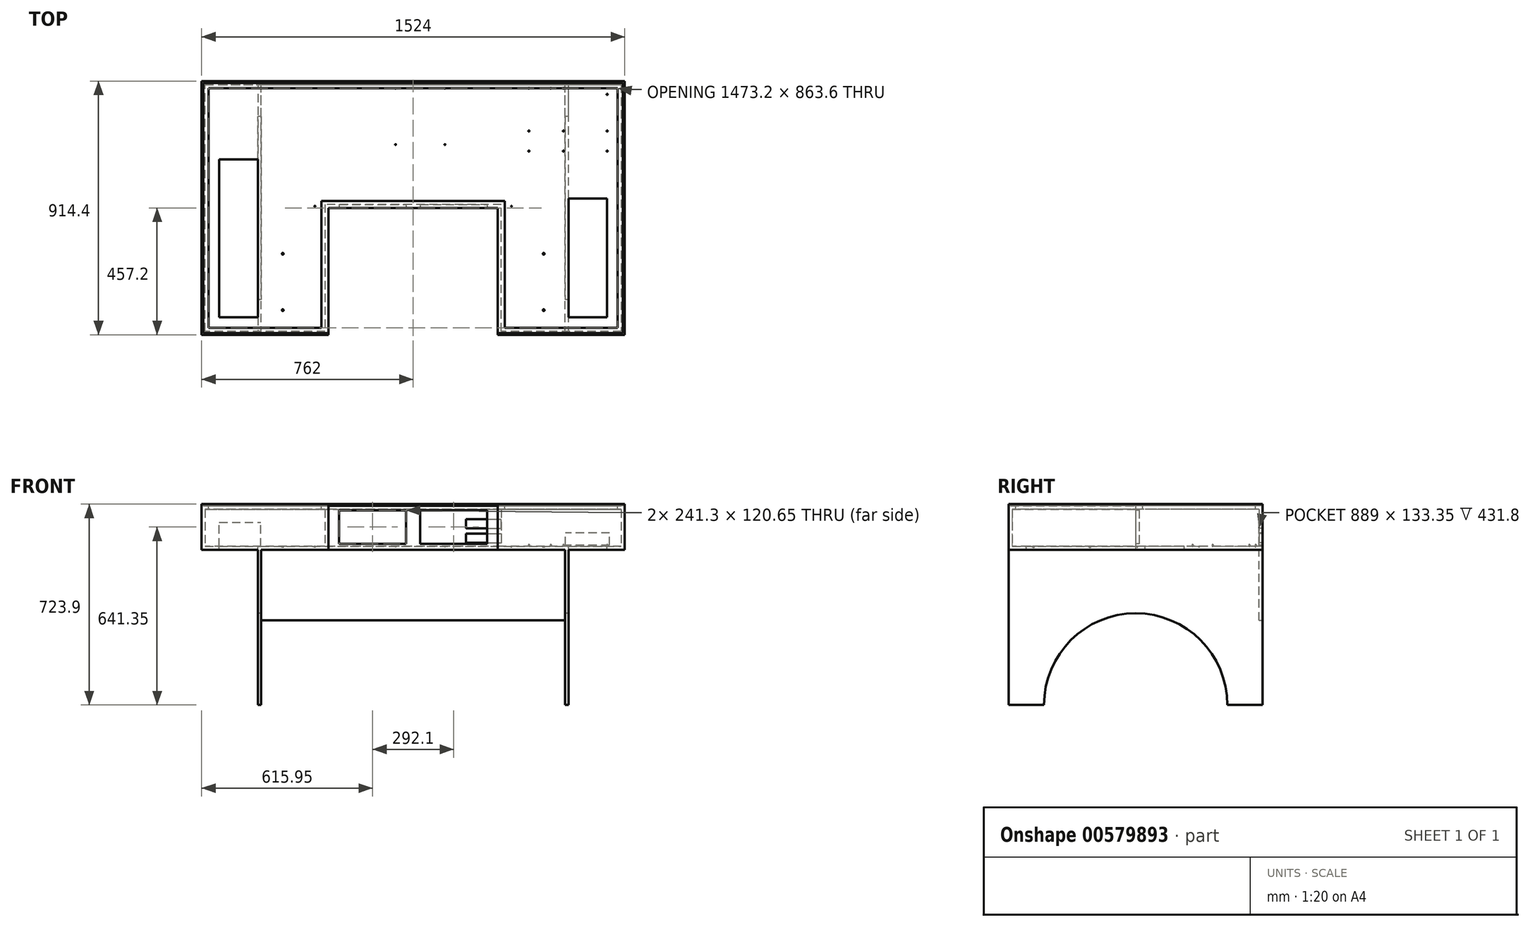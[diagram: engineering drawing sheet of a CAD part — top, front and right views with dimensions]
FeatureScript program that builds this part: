
annotation { "Feature Type Name" : "Feature", "Feature Type Description" : "" }
export const myFeature = defineFeature(function(context is Context, id is Id, definition is map)
    precondition{}
    {
        {
            var Q0;
            Q0=qCreatedBy(makeId("Top.planeOp"),FACE);
            var sketch = newSketch(context, id + "F0", { "sketchPlane" : qUnion([Q0])});
            skLineSegment(sketch, "E0.top", {"start": v(0, 914.4) * mm, "end": v(-1524, 914.4) * mm});
            skLineSegment(sketch, "E0.left", {"start": v(0, 0) * mm, "end": v(0, 914.4) * mm});
            skLineSegment(sketch, "E0.right", {"start": v(-1524, 0) * mm, "end": v(-1524, 914.4) * mm});
            skLineSegment(sketch, "E1.top", {"start": v(-1066.8, 457.2) * mm, "end": v(-457.2, 457.2) * mm});
            skLineSegment(sketch, "E1.left", {"start": v(-1066.8, 0) * mm, "end": v(-1066.8, 457.2) * mm});
            skLineSegment(sketch, "E1.right", {"start": v(-457.2, 0) * mm, "end": v(-457.2, 457.2) * mm});
            skLineSegment(sketch, "E2", {"start": v(-1524, 0) * mm, "end": v(-1066.8, 0) * mm});
            skLineSegment(sketch, "E3", {"start": v(-457.2, 0) * mm, "end": v(0, 0) * mm});
            skSolve(sketch);
        }
        {
            var Q0;
            Q0 = qSketchRegion(id + "F0", true);
            extrude(context, id + "F1", {"entities" : qUnion([Q0]), "depth" : 12.7 * mm, "offsetDistance" : 25.4 * mm});
        }
        {
            var Q0;
            Q0=makeQuery(id+"F1.opExtrude","CAP_FACE",FACE,{"disambiguationData":[OSD([sQuery(id+"F0.wireOp",EDGE,"E0.top"),sQuery(id+"F0.wireOp",EDGE,"E0.left"),sQuery(id+"F0.wireOp",EDGE,"E0.right"),sQuery(id+"F0.wireOp",EDGE,"E1.top"),sQuery(id+"F0.wireOp",EDGE,"E1.left"),sQuery(id+"F0.wireOp",EDGE,"E1.right"),sQuery(id+"F0.wireOp",EDGE,"E2"),sQuery(id+"F0.wireOp",EDGE,"E3")])],"isStart":false});
            var sketch = newSketch(context, id + "F2", { "sketchPlane" : qUnion([Q0])});
            skLineSegment(sketch, "E4", {"start": v(0, 0) * mm, "end": v(0, 914.4) * mm});
            skLineSegment(sketch, "E5", {"start": v(0, 914.4) * mm, "end": v(-1524, 914.4) * mm});
            skLineSegment(sketch, "E6", {"start": v(-1524, 914.4) * mm, "end": v(-1524, 0) * mm});
            skLineSegment(sketch, "E7", {"start": v(-1524, 0) * mm, "end": v(-1066.8, 0) * mm});
            skLineSegment(sketch, "E8", {"start": v(-1066.8, 0) * mm, "end": v(-1066.8, 457.2) * mm});
            skLineSegment(sketch, "E9", {"start": v(-1066.8, 457.2) * mm, "end": v(-457.2, 457.2) * mm});
            skLineSegment(sketch, "E10", {"start": v(-457.2, 457.2) * mm, "end": v(-457.2, 0) * mm});
            skLineSegment(sketch, "E11", {"start": v(-457.2, 0) * mm, "end": v(0, 0) * mm});
            skLineSegment(sketch, "E12", {"start": v(-12.7, 12.7) * mm, "end": v(-444.5, 12.7) * mm});
            skLineSegment(sketch, "E13", {"start": v(-444.5, 12.7) * mm, "end": v(-444.5, 469.9) * mm});
            skLineSegment(sketch, "E14", {"start": v(-444.5, 469.9) * mm, "end": v(-1079.5, 469.9) * mm});
            skLineSegment(sketch, "E15", {"start": v(-1079.5, 469.9) * mm, "end": v(-1079.5, 12.7) * mm});
            skLineSegment(sketch, "E16", {"start": v(-1079.5, 12.7) * mm, "end": v(-1511.3, 12.7) * mm});
            skLineSegment(sketch, "E17", {"start": v(-1511.3, 12.7) * mm, "end": v(-1511.3, 901.7) * mm});
            skLineSegment(sketch, "E18", {"start": v(-1511.3, 901.7) * mm, "end": v(-12.7, 901.7) * mm});
            skLineSegment(sketch, "E19", {"start": v(-12.7, 901.7) * mm, "end": v(-12.7, 12.7) * mm});
            skSolve(sketch);
        }
        {
            var Q0;
            Q0 = qSketchRegion(id + "F2", true);
            extrude(context, id + "F3", {"entities" : qUnion([Q0]), "operationType" : NewBodyOperationType.ADD, "depth" : 152.4 * mm, "offsetDistance" : 25.4 * mm});
        }
        {
            var Q0;
            Q0=makeQuery(id+"F1.opExtrude","CAP_FACE",FACE,{"disambiguationData":[OSD([sQuery(id+"F0.wireOp",EDGE,"E0.top"),sQuery(id+"F0.wireOp",EDGE,"E0.left"),sQuery(id+"F0.wireOp",EDGE,"E0.right"),sQuery(id+"F0.wireOp",EDGE,"E1.top"),sQuery(id+"F0.wireOp",EDGE,"E1.left"),sQuery(id+"F0.wireOp",EDGE,"E1.right"),sQuery(id+"F0.wireOp",EDGE,"E2"),sQuery(id+"F0.wireOp",EDGE,"E3")])],"isStart":false});
            var sketch = newSketch(context, id + "F4", { "sketchPlane" : qUnion([Q0])});
            skCircle(sketch, "E20", {"center": v(-345.44, 889.43) * mm, "radius": 1.98 * mm});
            skCircle(sketch, "E21", {"center": v(-345.44, 734.5) * mm, "radius": 1.98 * mm});
            skCircle(sketch, "E22", {"center": v(-345.44, 662.1) * mm, "radius": 1.98 * mm});
            skCircle(sketch, "E23", {"center": v(-266.7, 889.43) * mm, "radius": 1.98 * mm});
            skCircle(sketch, "E24", {"center": v(-220.98, 889.43) * mm, "radius": 1.98 * mm});
            skCircle(sketch, "E25", {"center": v(-220.98, 734.5) * mm, "radius": 1.98 * mm});
            skCircle(sketch, "E26", {"center": v(-220.98, 662.1) * mm, "radius": 1.98 * mm});
            skCircle(sketch, "E27", {"center": v(-63.5, 866.57) * mm, "radius": 1.98 * mm});
            skCircle(sketch, "E28", {"center": v(-63.5, 734.5) * mm, "radius": 1.98 * mm});
            skCircle(sketch, "E29", {"center": v(-63.5, 662.1) * mm, "radius": 1.98 * mm});
            skSolve(sketch);
        }
        {
            var Q0;
            Q0=makeQuery(id+"F4.imprint","IMPRINT",FACE,{"disambiguationData":[TD([[makeQuery(id+"F4.imprint","IMPRINT",EDGE,{"derivedFrom":sQuery(id+"F4.wireOp",EDGE,"E20")}),1.0]])]});
            var Q1;
            Q1=makeQuery(id+"F4.imprint","IMPRINT",FACE,{"disambiguationData":[TD([[makeQuery(id+"F4.imprint","IMPRINT",EDGE,{"derivedFrom":sQuery(id+"F4.wireOp",EDGE,"E23")}),1.0]])]});
            var Q2;
            Q2=makeQuery(id+"F4.imprint","IMPRINT",FACE,{"disambiguationData":[TD([[makeQuery(id+"F4.imprint","IMPRINT",EDGE,{"derivedFrom":sQuery(id+"F4.wireOp",EDGE,"E24")}),1.0]])]});
            var Q3;
            Q3=makeQuery(id+"F4.imprint","IMPRINT",FACE,{"disambiguationData":[TD([[makeQuery(id+"F4.imprint","IMPRINT",EDGE,{"derivedFrom":sQuery(id+"F4.wireOp",EDGE,"E27")}),1.0]])]});
            var Q4;
            Q4=makeQuery(id+"F4.imprint","IMPRINT",FACE,{"disambiguationData":[TD([[makeQuery(id+"F4.imprint","IMPRINT",EDGE,{"derivedFrom":sQuery(id+"F4.wireOp",EDGE,"E28")}),1.0]])]});
            var Q5;
            Q5=makeQuery(id+"F4.imprint","IMPRINT",FACE,{"disambiguationData":[TD([[makeQuery(id+"F4.imprint","IMPRINT",EDGE,{"derivedFrom":sQuery(id+"F4.wireOp",EDGE,"E25")}),1.0]])]});
            var Q6;
            Q6=makeQuery(id+"F4.imprint","IMPRINT",FACE,{"disambiguationData":[TD([[makeQuery(id+"F4.imprint","IMPRINT",EDGE,{"derivedFrom":sQuery(id+"F4.wireOp",EDGE,"E21")}),1.0]])]});
            var Q7;
            Q7=makeQuery(id+"F4.imprint","IMPRINT",FACE,{"disambiguationData":[TD([[makeQuery(id+"F4.imprint","IMPRINT",EDGE,{"derivedFrom":sQuery(id+"F4.wireOp",EDGE,"E22")}),1.0]])]});
            var Q8;
            Q8=makeQuery(id+"F4.imprint","IMPRINT",FACE,{"disambiguationData":[TD([[makeQuery(id+"F4.imprint","IMPRINT",EDGE,{"derivedFrom":sQuery(id+"F4.wireOp",EDGE,"E26")}),1.0]])]});
            var Q9;
            Q9=makeQuery(id+"F4.imprint","IMPRINT",FACE,{"disambiguationData":[TD([[makeQuery(id+"F4.imprint","IMPRINT",EDGE,{"derivedFrom":sQuery(id+"F4.wireOp",EDGE,"E29")}),1.0]])]});
            extrude(context, id + "F5", {"entities" : qUnion([Q0, Q1, Q2, Q3, Q4, Q5, Q6, Q7, Q8, Q9]), "operationType" : NewBodyOperationType.ADD, "depth" : 6.35 * mm, "offsetDistance" : 25.4 * mm});
        }
        {
            var Q0;
            Q0=makeQuery(id+"F3.opExtrude","SWEPT_FACE",FACE,{"disambiguationData":[OSD([sQuery(id+"F2.wireOp",EDGE,"E18")])]});
            var sketch = newSketch(context, id + "F6", { "sketchPlane" : qUnion([Q0])});
            skLineSegment(sketch, "E30.bottom", {"start": v(-54.71, 16.81) * mm, "end": v(-213.46, 16.81) * mm});
            skLineSegment(sketch, "E30.top", {"start": v(-54.71, 61.26) * mm, "end": v(-213.46, 61.26) * mm});
            skLineSegment(sketch, "E30.left", {"start": v(-54.71, 16.81) * mm, "end": v(-54.71, 61.26) * mm});
            skLineSegment(sketch, "E30.right", {"start": v(-213.46, 16.81) * mm, "end": v(-213.46, 61.26) * mm});
            skSolve(sketch);
        }
        {
            var Q0;
            Q0 = qSketchRegion(id + "F6", true);
            extrude(context, id + "F7", {"entities" : qUnion([Q0]), "operationType" : NewBodyOperationType.REMOVE, "oppositeDirection" : true, "depth" : 25.4 * mm, "offsetDistance" : 25.4 * mm});
        }
        {
            var Q0;
            Q0=makeQuery(id+"F3.opExtrude","SWEPT_FACE",FACE,{"disambiguationData":[OSD([sQuery(id+"F2.wireOp",EDGE,"E18")])]});
            var sketch = newSketch(context, id + "F8", { "sketchPlane" : qUnion([Q0])});
            skLineSegment(sketch, "E31.bottom", {"start": v(-571.5, 58.74) * mm, "end": v(-444.5, 58.74) * mm});
            skLineSegment(sketch, "E31.top", {"start": v(-571.5, 25.4) * mm, "end": v(-444.5, 25.4) * mm});
            skLineSegment(sketch, "E31.left", {"start": v(-571.5, 58.74) * mm, "end": v(-571.5, 25.4) * mm});
            skLineSegment(sketch, "E31.right", {"start": v(-444.5, 58.74) * mm, "end": v(-444.5, 25.4) * mm});
            skLineSegment(sketch, "E32.bottom", {"start": v(-571.5, 77.79) * mm, "end": v(-444.5, 77.79) * mm});
            skLineSegment(sketch, "E32.top", {"start": v(-571.5, 111.13) * mm, "end": v(-444.5, 111.13) * mm});
            skLineSegment(sketch, "E32.left", {"start": v(-571.5, 77.79) * mm, "end": v(-571.5, 111.13) * mm});
            skLineSegment(sketch, "E32.right", {"start": v(-444.5, 77.79) * mm, "end": v(-444.5, 111.13) * mm});
            skSolve(sketch);
        }
        {
            var Q0;
            Q0 = qSketchRegion(id + "F8", true);
            extrude(context, id + "F9", {"entities" : qUnion([Q0]), "operationType" : NewBodyOperationType.REMOVE, "oppositeDirection" : true, "depth" : 25.4 * mm, "offsetDistance" : 25.4 * mm});
        }
        {
            var Q0;
            Q0=makeQuery(id+"F1.opExtrude","CAP_FACE",FACE,{"disambiguationData":[OSD([sQuery(id+"F0.wireOp",EDGE,"E0.top"),sQuery(id+"F0.wireOp",EDGE,"E0.left"),sQuery(id+"F0.wireOp",EDGE,"E0.right"),sQuery(id+"F0.wireOp",EDGE,"E1.top"),sQuery(id+"F0.wireOp",EDGE,"E1.left"),sQuery(id+"F0.wireOp",EDGE,"E1.right"),sQuery(id+"F0.wireOp",EDGE,"E2"),sQuery(id+"F0.wireOp",EDGE,"E3")])],"isStart":false});
            var sketch = newSketch(context, id + "F10", { "sketchPlane" : qUnion([Q0])});
            skCircle(sketch, "E33", {"center": v(-647.7, 889) * mm, "radius": 1.59 * mm});
            skCircle(sketch, "E34", {"center": v(-647.7, 685.8) * mm, "radius": 1.59 * mm});
            skCircle(sketch, "E35", {"center": v(-825.5, 889) * mm, "radius": 1.59 * mm});
            skCircle(sketch, "E36", {"center": v(-825.5, 685.8) * mm, "radius": 1.59 * mm});
            skSolve(sketch);
        }
        {
            var Q0;
            Q0 = qSketchRegion(id + "F10", true);
            extrude(context, id + "F11", {"entities" : qUnion([Q0]), "operationType" : NewBodyOperationType.REMOVE, "oppositeDirection" : true, "depth" : 2.54 * mm, "offsetDistance" : 25.4 * mm});
        }
        {
            var Q0;
            Q0=makeQuery(id+"F1.opExtrude","CAP_FACE",FACE,{"disambiguationData":[OSD([sQuery(id+"F0.wireOp",EDGE,"E0.top"),sQuery(id+"F0.wireOp",EDGE,"E0.left"),sQuery(id+"F0.wireOp",EDGE,"E0.right"),sQuery(id+"F0.wireOp",EDGE,"E1.top"),sQuery(id+"F0.wireOp",EDGE,"E1.left"),sQuery(id+"F0.wireOp",EDGE,"E1.right"),sQuery(id+"F0.wireOp",EDGE,"E2"),sQuery(id+"F0.wireOp",EDGE,"E3")])],"isStart":false});
            var sketch = newSketch(context, id + "F12", { "sketchPlane" : qUnion([Q0])});
            skLineSegment(sketch, "E37.bottom", {"start": v(-1460.5, 631.75) * mm, "end": v(-1321.85, 631.75) * mm});
            skLineSegment(sketch, "E37.top", {"start": v(-1460.5, 63.5) * mm, "end": v(-1321.85, 63.5) * mm});
            skLineSegment(sketch, "E37.left", {"start": v(-1460.5, 631.75) * mm, "end": v(-1460.5, 63.5) * mm});
            skLineSegment(sketch, "E37.right", {"start": v(-1321.85, 631.75) * mm, "end": v(-1321.85, 63.5) * mm});
            skLineSegment(sketch, "E38.bottom", {"start": v(-202.15, 491.75) * mm, "end": v(-63.5, 491.75) * mm});
            skLineSegment(sketch, "E38.top", {"start": v(-202.15, 63.5) * mm, "end": v(-63.5, 63.5) * mm});
            skLineSegment(sketch, "E38.left", {"start": v(-202.15, 491.75) * mm, "end": v(-202.15, 63.5) * mm});
            skLineSegment(sketch, "E38.right", {"start": v(-63.5, 491.75) * mm, "end": v(-63.5, 63.5) * mm});
            skSolve(sketch);
        }
        {
            var Q0;
            Q0 = qSketchRegion(id + "F12", true);
            extrude(context, id + "F13", {"entities" : qUnion([Q0]), "operationType" : NewBodyOperationType.REMOVE, "endBound" : BoundingType.THROUGH_ALL, "oppositeDirection" : true, "depth" : 25.4 * mm, "offsetDistance" : 25.4 * mm});
        }
        {
            var Q0;
            Q0=makeQuery(id+"F1.opExtrude","CAP_FACE",FACE,{"disambiguationData":[OSD([sQuery(id+"F0.wireOp",EDGE,"E0.top"),sQuery(id+"F0.wireOp",EDGE,"E0.left"),sQuery(id+"F0.wireOp",EDGE,"E0.right"),sQuery(id+"F0.wireOp",EDGE,"E1.top"),sQuery(id+"F0.wireOp",EDGE,"E1.left"),sQuery(id+"F0.wireOp",EDGE,"E1.right"),sQuery(id+"F0.wireOp",EDGE,"E2"),sQuery(id+"F0.wireOp",EDGE,"E3")])],"isStart":false});
            var sketch = newSketch(context, id + "F14", { "sketchPlane" : qUnion([Q0])});
            skCircle(sketch, "E39", {"center": v(-1231.9, 88.9) * mm, "radius": 3.18 * mm});
            skCircle(sketch, "E40", {"center": v(-1231.9, 292.1) * mm, "radius": 3.18 * mm});
            skCircle(sketch, "E41", {"center": v(-292.1, 292.1) * mm, "radius": 3.18 * mm});
            skCircle(sketch, "E42", {"center": v(-292.1, 88.9) * mm, "radius": 3.18 * mm});
            skSolve(sketch);
        }
        {
            var Q0;
            Q0 = qSketchRegion(id + "F14", true);
            extrude(context, id + "F15", {"entities" : qUnion([Q0]), "operationType" : NewBodyOperationType.REMOVE, "oppositeDirection" : true, "depth" : 3.17 * mm, "offsetDistance" : 25.4 * mm});
        }
        {
            var Q0;
            Q0=makeQuery(id+"F1.opExtrude","CAP_FACE",FACE,{"disambiguationData":[OSD([sQuery(id+"F0.wireOp",EDGE,"E0.top"),sQuery(id+"F0.wireOp",EDGE,"E0.left"),sQuery(id+"F0.wireOp",EDGE,"E0.right"),sQuery(id+"F0.wireOp",EDGE,"E1.top"),sQuery(id+"F0.wireOp",EDGE,"E1.left"),sQuery(id+"F0.wireOp",EDGE,"E1.right"),sQuery(id+"F0.wireOp",EDGE,"E2"),sQuery(id+"F0.wireOp",EDGE,"E3")])],"isStart":false});
            var sketch = newSketch(context, id + "F16", { "sketchPlane" : qUnion([Q0])});
            skCircle(sketch, "E43", {"center": v(-1116.01, 463.55) * mm, "radius": 1.59 * mm});
            skCircle(sketch, "E44", {"center": v(-407.99, 463.55) * mm, "radius": 1.59 * mm});
            skSolve(sketch);
        }
        {
            var Q0;
            Q0 = qSketchRegion(id + "F16", true);
            extrude(context, id + "F17", {"entities" : qUnion([Q0]), "operationType" : NewBodyOperationType.REMOVE, "oppositeDirection" : true, "depth" : 3.17 * mm, "offsetDistance" : 25.4 * mm});
        }
        {
            var Q0;
            Q0=makeQuery(id+"F3.opExtrude","SWEPT_FACE",FACE,{"disambiguationData":[OSD([sQuery(id+"F2.wireOp",EDGE,"E18")])]});
            var sketch = newSketch(context, id + "F18", { "sketchPlane" : qUnion([Q0])});
            skLineSegment(sketch, "E45.bottom", {"start": v(-1460.5, 12.7) * mm, "end": v(-1310.39, 12.7) * mm});
            skLineSegment(sketch, "E45.top", {"start": v(-1460.5, 98.8) * mm, "end": v(-1310.39, 98.8) * mm});
            skLineSegment(sketch, "E45.left", {"start": v(-1460.5, 12.7) * mm, "end": v(-1460.5, 98.8) * mm});
            skLineSegment(sketch, "E45.right", {"start": v(-1310.39, 12.7) * mm, "end": v(-1310.39, 98.8) * mm});
            skSolve(sketch);
        }
        {
            var Q0;
            Q0 = qSketchRegion(id + "F18", true);
            extrude(context, id + "F19", {"entities" : qUnion([Q0]), "operationType" : NewBodyOperationType.REMOVE, "oppositeDirection" : true, "depth" : 25.4 * mm, "offsetDistance" : 25.4 * mm});
        }
        {
            var Q0;
            Q0=makeQuery(id+"F3.opExtrude","CAP_FACE",FACE,{"disambiguationData":[OSD([sQuery(id+"F2.wireOp",EDGE,"E4"),sQuery(id+"F2.wireOp",EDGE,"E5"),sQuery(id+"F2.wireOp",EDGE,"E6"),sQuery(id+"F2.wireOp",EDGE,"E7"),sQuery(id+"F2.wireOp",EDGE,"E8"),sQuery(id+"F2.wireOp",EDGE,"E9"),sQuery(id+"F2.wireOp",EDGE,"E10"),sQuery(id+"F2.wireOp",EDGE,"E11"),sQuery(id+"F2.wireOp",EDGE,"E12"),sQuery(id+"F2.wireOp",EDGE,"E13"),sQuery(id+"F2.wireOp",EDGE,"E14"),sQuery(id+"F2.wireOp",EDGE,"E15"),sQuery(id+"F2.wireOp",EDGE,"E16"),sQuery(id+"F2.wireOp",EDGE,"E17"),sQuery(id+"F2.wireOp",EDGE,"E18"),sQuery(id+"F2.wireOp",EDGE,"E19")])],"isStart":false});
            var sketch = newSketch(context, id + "F20", { "sketchPlane" : qUnion([Q0])});
            skLineSegment(sketch, "E46", {"start": v(-1511.3, 12.7) * mm, "end": v(-1079.5, 12.7) * mm});
            skLineSegment(sketch, "E47", {"start": v(-1079.5, 12.7) * mm, "end": v(-1079.5, 469.9) * mm});
            skLineSegment(sketch, "E48", {"start": v(-1079.5, 469.9) * mm, "end": v(-444.5, 469.9) * mm});
            skLineSegment(sketch, "E49", {"start": v(-444.5, 469.9) * mm, "end": v(-444.5, 12.7) * mm});
            skLineSegment(sketch, "E50", {"start": v(-444.5, 12.7) * mm, "end": v(-12.7, 12.7) * mm});
            skLineSegment(sketch, "E51", {"start": v(-12.7, 12.7) * mm, "end": v(-12.7, 901.7) * mm});
            skLineSegment(sketch, "E52", {"start": v(-12.7, 901.7) * mm, "end": v(-1511.3, 901.7) * mm});
            skLineSegment(sketch, "E53", {"start": v(-1511.3, 901.7) * mm, "end": v(-1511.3, 12.7) * mm});
            skLineSegment(sketch, "E54", {"start": v(-1517.65, 6.35) * mm, "end": v(-1073.15, 6.35) * mm});
            skLineSegment(sketch, "E55", {"start": v(-1073.15, 6.35) * mm, "end": v(-1073.15, 463.55) * mm});
            skLineSegment(sketch, "E56", {"start": v(-1073.15, 463.55) * mm, "end": v(-450.85, 463.55) * mm});
            skLineSegment(sketch, "E57", {"start": v(-450.85, 463.55) * mm, "end": v(-450.85, 6.35) * mm});
            skLineSegment(sketch, "E58", {"start": v(-450.85, 6.35) * mm, "end": v(-6.35, 6.35) * mm});
            skLineSegment(sketch, "E59", {"start": v(-6.35, 6.35) * mm, "end": v(-6.35, 908.05) * mm});
            skLineSegment(sketch, "E60", {"start": v(-6.35, 908.05) * mm, "end": v(-1517.65, 908.05) * mm});
            skLineSegment(sketch, "E61", {"start": v(-1517.65, 908.05) * mm, "end": v(-1517.65, 6.35) * mm});
            skSolve(sketch);
        }
        {
            var Q0;
            Q0 = qSketchRegion(id + "F20", true);
            extrude(context, id + "F21", {"entities" : qUnion([Q0]), "operationType" : NewBodyOperationType.REMOVE, "oppositeDirection" : true, "depth" : 6.35 * mm, "offsetDistance" : 25.4 * mm});
        }
        {
            var Q0;
            Q0=makeQuery(id+"F21.boolean.opBoolean","COPY",FACE,{"derivedFrom":makeQuery(id+"F21.opExtrude","CAP_FACE",FACE,{"disambiguationData":[OSD([sQuery(id+"F20.wireOp",EDGE,"E46"),sQuery(id+"F20.wireOp",EDGE,"E47"),sQuery(id+"F20.wireOp",EDGE,"E48"),sQuery(id+"F20.wireOp",EDGE,"E49"),sQuery(id+"F20.wireOp",EDGE,"E50"),sQuery(id+"F20.wireOp",EDGE,"E51"),sQuery(id+"F20.wireOp",EDGE,"E52"),sQuery(id+"F20.wireOp",EDGE,"E53"),sQuery(id+"F20.wireOp",EDGE,"E54"),sQuery(id+"F20.wireOp",EDGE,"E55"),sQuery(id+"F20.wireOp",EDGE,"E56"),sQuery(id+"F20.wireOp",EDGE,"E57"),sQuery(id+"F20.wireOp",EDGE,"E58"),sQuery(id+"F20.wireOp",EDGE,"E59"),sQuery(id+"F20.wireOp",EDGE,"E60"),sQuery(id+"F20.wireOp",EDGE,"E61")])],"isStart":false})});
            var sketch = newSketch(context, id + "F22", { "sketchPlane" : qUnion([Q0])});
            skLineSegment(sketch, "E62", {"start": v(-1511.3, 12.7) * mm, "end": v(-1079.5, 12.7) * mm});
            skLineSegment(sketch, "E63", {"start": v(-1079.5, 12.7) * mm, "end": v(-1079.5, 469.9) * mm});
            skLineSegment(sketch, "E64", {"start": v(-1079.5, 469.9) * mm, "end": v(-444.5, 469.9) * mm});
            skLineSegment(sketch, "E65", {"start": v(-444.5, 469.9) * mm, "end": v(-444.5, 12.7) * mm});
            skLineSegment(sketch, "E66", {"start": v(-444.5, 12.7) * mm, "end": v(-12.7, 12.7) * mm});
            skLineSegment(sketch, "E67", {"start": v(-12.7, 12.7) * mm, "end": v(-12.7, 901.7) * mm});
            skLineSegment(sketch, "E68", {"start": v(-12.7, 901.7) * mm, "end": v(-1511.3, 901.7) * mm});
            skLineSegment(sketch, "E69", {"start": v(-1511.3, 901.7) * mm, "end": v(-1511.3, 12.7) * mm});
            skLineSegment(sketch, "E70", {"start": v(-1498.6, 25.4) * mm, "end": v(-1092.2, 25.4) * mm});
            skLineSegment(sketch, "E71", {"start": v(-1092.2, 25.4) * mm, "end": v(-1092.2, 482.6) * mm});
            skLineSegment(sketch, "E72", {"start": v(-1092.2, 482.6) * mm, "end": v(-431.8, 482.6) * mm});
            skLineSegment(sketch, "E73", {"start": v(-431.8, 482.6) * mm, "end": v(-431.8, 25.4) * mm});
            skLineSegment(sketch, "E74", {"start": v(-431.8, 25.4) * mm, "end": v(-25.4, 25.4) * mm});
            skLineSegment(sketch, "E75", {"start": v(-25.4, 25.4) * mm, "end": v(-25.4, 889) * mm});
            skLineSegment(sketch, "E76", {"start": v(-25.4, 889) * mm, "end": v(-1498.6, 889) * mm});
            skLineSegment(sketch, "E77", {"start": v(-1498.6, 889) * mm, "end": v(-1498.6, 25.4) * mm});
            skSolve(sketch);
        }
        {
            var Q0;
            Q0 = qSketchRegion(id + "F22", true);
            extrude(context, id + "F23", {"entities" : qUnion([Q0]), "operationType" : NewBodyOperationType.ADD, "oppositeDirection" : true, "depth" : 12.7 * mm, "offsetDistance" : 25.4 * mm});
        }
        {
            var Q0;
            Q0=makeQuery(id+"F3.boolean.opBoolean","MERGE",FACE,{"derivedFrom":[makeQuery(id+"F1.opExtrude","SWEPT_FACE",FACE,{"disambiguationData":[OSD([sQuery(id+"F0.wireOp",EDGE,"E1.top")])]}),makeQuery(id+"F3.opExtrude","SWEPT_FACE",FACE,{"disambiguationData":[OSD([sQuery(id+"F2.wireOp",EDGE,"E9")])]})]});
            var sketch = newSketch(context, id + "F24", { "sketchPlane" : qUnion([Q0])});
            skLineSegment(sketch, "E78.bottom", {"start": v(-1028.7, 142.87) * mm, "end": v(-787.4, 142.87) * mm});
            skLineSegment(sketch, "E78.top", {"start": v(-1028.7, 22.22) * mm, "end": v(-787.4, 22.22) * mm});
            skLineSegment(sketch, "E78.left", {"start": v(-1028.7, 142.87) * mm, "end": v(-1028.7, 22.22) * mm});
            skLineSegment(sketch, "E78.right", {"start": v(-787.4, 142.87) * mm, "end": v(-787.4, 22.22) * mm});
            skLineSegment(sketch, "E79.bottom", {"start": v(-736.6, 142.88) * mm, "end": v(-495.3, 142.88) * mm});
            skLineSegment(sketch, "E79.top", {"start": v(-736.6, 22.23) * mm, "end": v(-495.3, 22.23) * mm});
            skLineSegment(sketch, "E79.left", {"start": v(-736.6, 142.88) * mm, "end": v(-736.6, 22.23) * mm});
            skLineSegment(sketch, "E79.right", {"start": v(-495.3, 142.88) * mm, "end": v(-495.3, 22.23) * mm});
            skSolve(sketch);
        }
        {
            var Q0;
            Q0 = qSketchRegion(id + "F24", true);
            extrude(context, id + "F25", {"entities" : qUnion([Q0]), "operationType" : NewBodyOperationType.REMOVE, "oppositeDirection" : true, "depth" : 25.4 * mm, "offsetDistance" : 25.4 * mm});
        }
        {
            var Q0;
            Q0=makeQuery(id+"F1.opExtrude","CAP_FACE",FACE,{"disambiguationData":[OSD([sQuery(id+"F0.wireOp",EDGE,"E0.top"),sQuery(id+"F0.wireOp",EDGE,"E0.left"),sQuery(id+"F0.wireOp",EDGE,"E0.right"),sQuery(id+"F0.wireOp",EDGE,"E1.top"),sQuery(id+"F0.wireOp",EDGE,"E1.left"),sQuery(id+"F0.wireOp",EDGE,"E1.right"),sQuery(id+"F0.wireOp",EDGE,"E2"),sQuery(id+"F0.wireOp",EDGE,"E3")])],"isStart":true});
            var sketch = newSketch(context, id + "F26", { "sketchPlane" : qUnion([Q0])});
            skLineSegment(sketch, "E80.bottom", {"start": v(-1321.85, 0) * mm, "end": v(-1309.15, 0) * mm});
            skLineSegment(sketch, "E80.top", {"start": v(-1321.85, -914.4) * mm, "end": v(-1309.15, -914.4) * mm});
            skLineSegment(sketch, "E80.left", {"start": v(-1321.85, 0) * mm, "end": v(-1321.85, -914.4) * mm});
            skLineSegment(sketch, "E80.right", {"start": v(-1309.15, 0) * mm, "end": v(-1309.15, -914.4) * mm});
            skLineSegment(sketch, "E81.bottom", {"start": v(-202.15, 0) * mm, "end": v(-214.85, 0) * mm});
            skLineSegment(sketch, "E81.top", {"start": v(-202.15, -914.4) * mm, "end": v(-214.85, -914.4) * mm});
            skLineSegment(sketch, "E81.left", {"start": v(-202.15, 0) * mm, "end": v(-202.15, -914.4) * mm});
            skLineSegment(sketch, "E81.right", {"start": v(-214.85, 0) * mm, "end": v(-214.85, -914.4) * mm});
            skSolve(sketch);
        }
        {
            var Q0;
            Q0 = qSketchRegion(id + "F26", true);
            extrude(context, id + "F27", {"entities" : qUnion([Q0]), "operationType" : NewBodyOperationType.ADD, "depth" : 558.8 * mm, "offsetDistance" : 25.4 * mm});
        }
        {
            var Q0;
            {var subQ0=sQuery(id+"F0.wireOp",EDGE,"E1.right");var subQ1=sQuery(id+"F0.wireOp",EDGE,"E3");var subQ2=sQuery(id+"F0.wireOp",EDGE,"E2");var subQ3=sQuery(id+"F0.wireOp",EDGE,"E0.top");var subQ4=sQuery(id+"F0.wireOp",EDGE,"E1.top");var subQ5=sQuery(id+"F0.wireOp",EDGE,"E1.left");Q0=makeQuery(id+"F27.boolean.opBoolean","SPLIT",FACE,{"disambiguationData":[TD([makeQuery(id+"F1.opExtrude","SWEPT_FACE",FACE,{"disambiguationData":[OSD([subQ4])]})])],"derivedFrom":makeQuery(id+"F1.opExtrude","CAP_FACE",FACE,{"disambiguationData":[OSD([subQ3,sQuery(id+"F0.wireOp",EDGE,"E0.left"),sQuery(id+"F0.wireOp",EDGE,"E0.right"),subQ4,subQ5,subQ0,subQ2,subQ1])],"isStart":true})});}
            var sketch = newSketch(context, id + "F28", { "sketchPlane" : qUnion([Q0])});
            skLineSegment(sketch, "E82.bottom", {"start": v(-1309.15, -914.4) * mm, "end": v(-214.85, -914.4) * mm});
            skLineSegment(sketch, "E82.top", {"start": v(-1309.15, -901.7) * mm, "end": v(-214.85, -901.7) * mm});
            skLineSegment(sketch, "E82.left", {"start": v(-1309.15, -914.4) * mm, "end": v(-1309.15, -901.7) * mm});
            skLineSegment(sketch, "E82.right", {"start": v(-214.85, -914.4) * mm, "end": v(-214.85, -901.7) * mm});
            skSolve(sketch);
        }
        {
            var Q0;
            Q0 = qSketchRegion(id + "F28", true);
            extrude(context, id + "F29", {"entities" : qUnion([Q0]), "operationType" : NewBodyOperationType.ADD, "depth" : 254 * mm, "offsetDistance" : 25.4 * mm});
        }
        {
            var Q0;
            Q0=makeQuery(id+"F27.boolean.opBoolean","MERGE",FACE,{"derivedFrom":[makeQuery(id+"F13.boolean.opBoolean","COPY",FACE,{"derivedFrom":makeQuery(id+"F13.opExtrude","SWEPT_FACE",FACE,{"disambiguationData":[OSD([sQuery(id+"F12.wireOp",EDGE,"E37.right")])]})}),makeQuery(id+"F27.opExtrude","SWEPT_FACE",FACE,{"disambiguationData":[OSD([sQuery(id+"F26.wireOp",EDGE,"E80.left")])]})]});
            var sketch = newSketch(context, id + "F30", { "sketchPlane" : qUnion([Q0])});
            skPoint(sketch, "E83", {"position": v(-787.4, -558.8) * mm});
            skPoint(sketch, "E84", {"position": v(-127, -558.8) * mm});
            skArc(sketch, "E85", {"start": v(-127, -558.8) * mm, "mid": v(-457.2, -228.6) * mm, "end": v(-787.4, -558.8) * mm});
            skSolve(sketch);
        }
        {
            var Q0;
            {var subQ0=sQuery(id+"F30.wireOp",EDGE,"E85");Q0=makeQuery(id+"F30.imprint","IMPRINT",FACE,{"disambiguationData":[TD([[makeQuery(id+"F30.imprint","IMPRINT",EDGE,{"derivedFrom":subQ0}),1.0]])]});}
            extrude(context, id + "F31", {"entities" : qUnion([Q0]), "operationType" : NewBodyOperationType.REMOVE, "endBound" : BoundingType.THROUGH_ALL, "oppositeDirection" : true, "depth" : 762 * mm, "offsetDistance" : 25.4 * mm});
        }
        {
            var Q0;
            Q0=makeQuery(id+"F23.boolean.opBoolean","MERGE",FACE,{"derivedFrom":[makeQuery(id+"F21.boolean.opBoolean","COPY",FACE,{"derivedFrom":makeQuery(id+"F21.opExtrude","CAP_FACE",FACE,{"disambiguationData":[OSD([sQuery(id+"F20.wireOp",EDGE,"E46"),sQuery(id+"F20.wireOp",EDGE,"E47"),sQuery(id+"F20.wireOp",EDGE,"E48"),sQuery(id+"F20.wireOp",EDGE,"E49"),sQuery(id+"F20.wireOp",EDGE,"E50"),sQuery(id+"F20.wireOp",EDGE,"E51"),sQuery(id+"F20.wireOp",EDGE,"E52"),sQuery(id+"F20.wireOp",EDGE,"E53"),sQuery(id+"F20.wireOp",EDGE,"E54"),sQuery(id+"F20.wireOp",EDGE,"E55"),sQuery(id+"F20.wireOp",EDGE,"E56"),sQuery(id+"F20.wireOp",EDGE,"E57"),sQuery(id+"F20.wireOp",EDGE,"E58"),sQuery(id+"F20.wireOp",EDGE,"E59"),sQuery(id+"F20.wireOp",EDGE,"E60"),sQuery(id+"F20.wireOp",EDGE,"E61")])],"isStart":false})}),makeQuery(id+"F23.opExtrude","CAP_FACE",FACE,{"disambiguationData":[OSD([sQuery(id+"F22.wireOp",EDGE,"E62"),sQuery(id+"F22.wireOp",EDGE,"E63"),sQuery(id+"F22.wireOp",EDGE,"E64"),sQuery(id+"F22.wireOp",EDGE,"E65"),sQuery(id+"F22.wireOp",EDGE,"E66"),sQuery(id+"F22.wireOp",EDGE,"E67"),sQuery(id+"F22.wireOp",EDGE,"E68"),sQuery(id+"F22.wireOp",EDGE,"E69"),sQuery(id+"F22.wireOp",EDGE,"E70"),sQuery(id+"F22.wireOp",EDGE,"E71"),sQuery(id+"F22.wireOp",EDGE,"E72"),sQuery(id+"F22.wireOp",EDGE,"E73"),sQuery(id+"F22.wireOp",EDGE,"E74"),sQuery(id+"F22.wireOp",EDGE,"E75"),sQuery(id+"F22.wireOp",EDGE,"E76"),sQuery(id+"F22.wireOp",EDGE,"E77")])],"isStart":true})]});
            var sketch = newSketch(context, id + "F32", { "sketchPlane" : qUnion([Q0])});
            skLineSegment(sketch, "E86.bottom", {"start": v(-1073.15, 6.35) * mm, "end": v(-450.85, 6.35) * mm});
            skLineSegment(sketch, "E86.top", {"start": v(-1073.15, 463.55) * mm, "end": v(-450.85, 463.55) * mm});
            skLineSegment(sketch, "E86.left", {"start": v(-1073.15, 6.35) * mm, "end": v(-1073.15, 463.55) * mm});
            skLineSegment(sketch, "E86.right", {"start": v(-450.85, 6.35) * mm, "end": v(-450.85, 463.55) * mm});
            skSolve(sketch);
        }
        {
            var Q0;
            Q0 = qSketchRegion(id + "F32", true);
            extrude(context, id + "F33", {"entities" : qUnion([Q0]), "operationType" : NewBodyOperationType.REMOVE, "depth" : 25.4 * mm, "offsetDistance" : 25.4 * mm});
        }
    });
